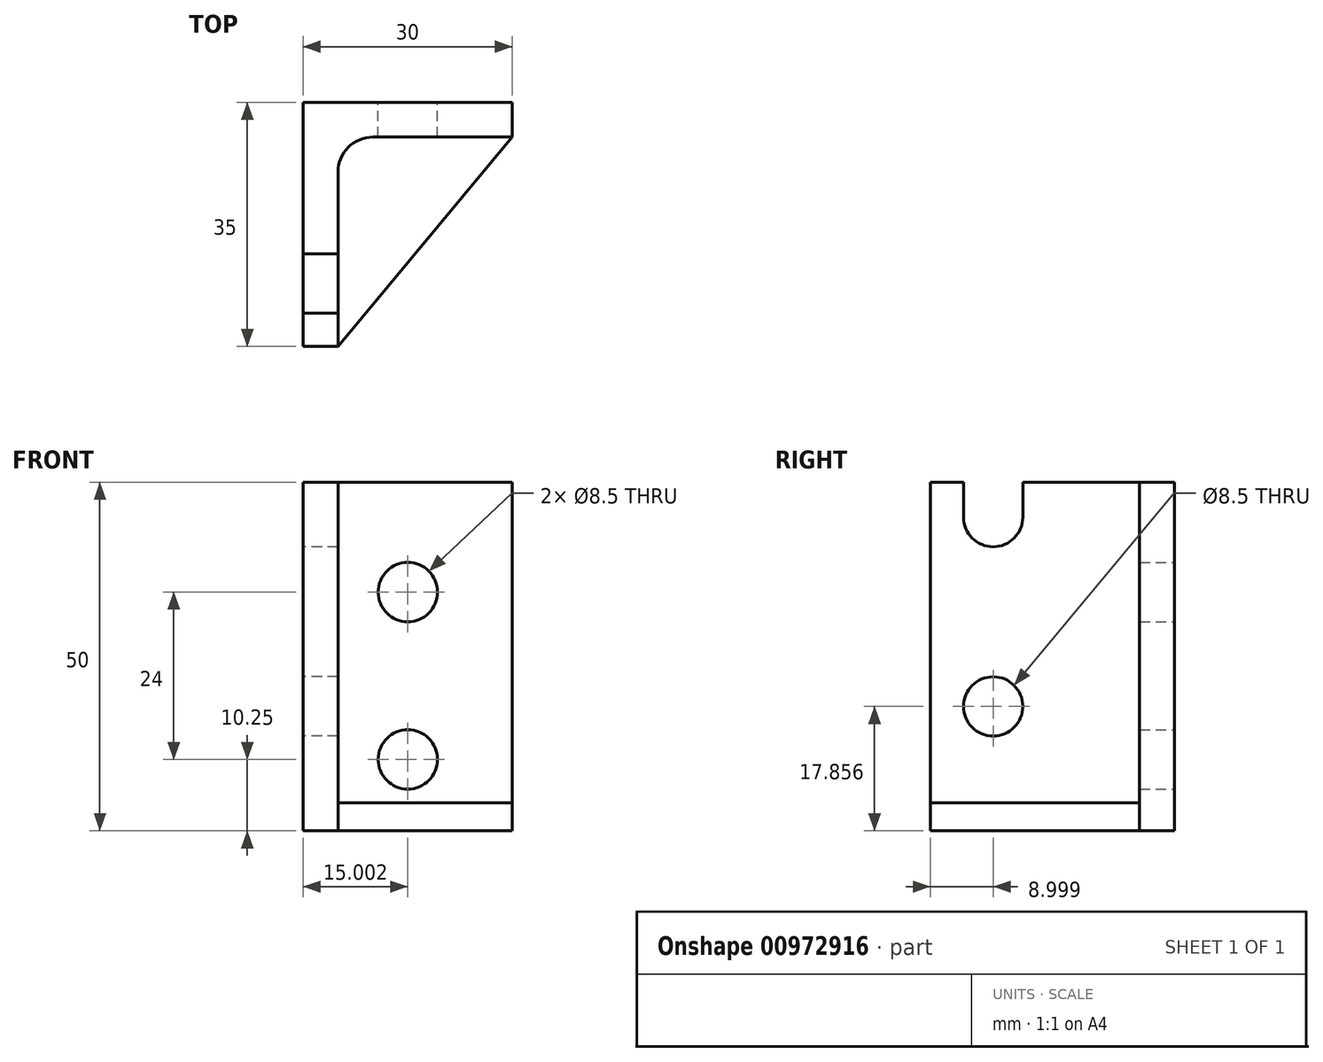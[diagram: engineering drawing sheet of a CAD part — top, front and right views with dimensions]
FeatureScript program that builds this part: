
annotation { "Feature Type Name" : "Feature", "Feature Type Description" : "" }
export const myFeature = defineFeature(function(context is Context, id is Id, definition is map)
    precondition{}
    {
        {
            var Q0;
            Q0=qCreatedBy(makeId("Top.planeOp"),FACE);
            var sketch = newSketch(context, id + "F0", { "sketchPlane" : qUnion([Q0])});
            skLineSegment(sketch, "E0", {"start": v(-9.75, -4.4) * mm, "end": v(-9.75, 25.6) * mm});
            skLineSegment(sketch, "E1", {"start": v(-9.75, 25.6) * mm, "end": v(15.25, 25.6) * mm});
            skLineSegment(sketch, "E2", {"start": v(-9.75, -4.4) * mm, "end": v(-14.75, -4.4) * mm});
            skLineSegment(sketch, "E3", {"start": v(-14.75, -4.4) * mm, "end": v(-14.75, 30.6) * mm});
            skLineSegment(sketch, "E4", {"start": v(-14.75, 30.6) * mm, "end": v(15.25, 30.6) * mm});
            skLineSegment(sketch, "E5", {"start": v(15.25, 30.6) * mm, "end": v(15.25, 25.6) * mm});
            skLineSegment(sketch, "E6", {"start": v(-9.75, -4.4) * mm, "end": v(15.25, 25.6) * mm});
            skSolve(sketch);
        }
        {
            var Q0;
            Q0=makeQuery(id+"F0.imprint","IMPRINT",FACE,{"disambiguationData":[TD([[makeQuery(id+"F0.imprint","IMPRINT",EDGE,{"derivedFrom":sQuery(id+"F0.wireOp",EDGE,"E0")}),1.0]])]});
            extrude(context, id + "F1", {"entities" : qUnion([Q0]), "depth" : 50 * mm, "offsetDistance" : 25 * mm});
        }
        {
            var Q0;
            Q0=makeQuery(id+"F0.imprint","IMPRINT",FACE,{"disambiguationData":[TD([[makeQuery(id+"F0.imprint","IMPRINT",EDGE,{"derivedFrom":sQuery(id+"F0.wireOp",EDGE,"E0")}),-1.0]])]});
            extrude(context, id + "F2", {"entities" : qUnion([Q0]), "operationType" : NewBodyOperationType.ADD, "depth" : 4 * mm, "offsetDistance" : 25 * mm});
        }
        {
            var Q0;
            Q0=makeQuery(id+"F1.opExtrude","SWEPT_FACE",FACE,{"disambiguationData":[OSD([sQuery(id+"F0.wireOp",EDGE,"E3")])]});
            var sketch = newSketch(context, id + "F3", { "sketchPlane" : qUnion([Q0])});
            skLineSegment(sketch, "E7.0.0", {"start": v(-30.6, 0) * mm, "end": v(4.4, 0) * mm});
            skLineSegment(sketch, "E7.0.1", {"start": v(4.4, 0) * mm, "end": v(4.4, 50) * mm});
            skLineSegment(sketch, "E7.0.2", {"start": v(4.4, 50) * mm, "end": v(-30.6, 50) * mm});
            skLineSegment(sketch, "E7.0.3", {"start": v(-30.6, 50) * mm, "end": v(-30.6, 0) * mm});
            skLineSegment(sketch, "E8", {"start": v(-30.6, 20) * mm, "end": v(4.4, 20) * mm, "construction": true});
            skLineSegment(sketch, "E9", {"start": v(-30.6, 45) * mm, "end": v(4.4, 45) * mm, "construction": true});
            skCircle(sketch, "E10", {"center": v(-4.6, 17.86) * mm, "radius": 4.25 * mm});
            skCircle(sketch, "E11", {"center": v(-4.6, 45) * mm, "radius": 4.25 * mm});
            skLineSegment(sketch, "E12", {"start": v(-0.35, 45) * mm, "end": v(-0.35, 50) * mm});
            skLineSegment(sketch, "E13", {"start": v(-8.85, 45) * mm, "end": v(-8.85, 50) * mm});
            skSolve(sketch);
        }
        {
            var Q0;
            Q0=makeQuery(id+"F3.imprint","IMPRINT",FACE,{"disambiguationData":[TD([[makeQuery(id+"F3.imprint","IMPRINT",EDGE,{"derivedFrom":sQuery(id+"F3.wireOp",EDGE,"E10")}),1.0]])]});
            var Q1;
            {var subQ0=sQuery(id+"F3.wireOp",EDGE,"E11");var subQ1=makeQuery(id+"F3.imprint","INTERSECT",VERTEX,{"derivedFrom":[subQ0,sQuery(id+"F3.wireOp",EDGE,"E12")]});Q1=makeQuery(id+"F3.imprint","IMPRINT",FACE,{"disambiguationData":[TD([[makeQuery(id+"F3.imprint","IMPRINT",EDGE,{"disambiguationData":[TD([[subQ1,-1.0]])],"derivedFrom":subQ0}),1.0]])]});}
            var Q2;
            {var subQ0=sQuery(id+"F3.wireOp",EDGE,"E12");Q2=makeQuery(id+"F3.imprint","IMPRINT",FACE,{"disambiguationData":[TD([[makeQuery(id+"F3.imprint","IMPRINT",EDGE,{"derivedFrom":subQ0}),1.0]])]});}
            extrude(context, id + "F4", {"entities" : qUnion([Q0, Q1, Q2]), "operationType" : NewBodyOperationType.REMOVE, "oppositeDirection" : true, "depth" : 25 * mm, "offsetDistance" : 25 * mm});
        }
        {
            var Q0;
            Q0=makeQuery(id+"F1.opExtrude","SWEPT_FACE",FACE,{"disambiguationData":[OSD([sQuery(id+"F0.wireOp",EDGE,"E4")])]});
            var sketch = newSketch(context, id + "F5", { "sketchPlane" : qUnion([Q0])});
            skLineSegment(sketch, "E14.0.0", {"start": v(-15.25, 0) * mm, "end": v(14.75, 0) * mm});
            skLineSegment(sketch, "E14.0.1", {"start": v(14.75, 0) * mm, "end": v(14.75, 50) * mm});
            skLineSegment(sketch, "E14.0.2", {"start": v(14.75, 50) * mm, "end": v(-15.25, 50) * mm});
            skLineSegment(sketch, "E14.0.3", {"start": v(-15.25, 50) * mm, "end": v(-15.25, 0) * mm});
            skCircle(sketch, "E15", {"center": v(-0.25, 10.25) * mm, "radius": 4.25 * mm});
            skCircle(sketch, "E16", {"center": v(-0.25, 34.25) * mm, "radius": 4.25 * mm});
            skPoint(sketch, "E17", {"position": v(-0.25, 0) * mm});
            skSolve(sketch);
        }
        {
            var Q0;
            Q0=makeQuery(id+"F5.imprint","IMPRINT",FACE,{"disambiguationData":[TD([[makeQuery(id+"F5.imprint","IMPRINT",EDGE,{"derivedFrom":sQuery(id+"F5.wireOp",EDGE,"E16")}),1.0]])]});
            var Q1;
            Q1=makeQuery(id+"F5.imprint","IMPRINT",FACE,{"disambiguationData":[TD([[makeQuery(id+"F5.imprint","IMPRINT",EDGE,{"derivedFrom":sQuery(id+"F5.wireOp",EDGE,"E15")}),1.0]])]});
            extrude(context, id + "F6", {"entities" : qUnion([Q0, Q1]), "operationType" : NewBodyOperationType.REMOVE, "oppositeDirection" : true, "depth" : 25 * mm, "offsetDistance" : 25 * mm});
        }
        {
            var Q0;
            Q0=makeQuery(id+"F1.opExtrude","SWEPT_EDGE",EDGE,{"disambiguationData":[OSD([sQuery(id+"F0.wireOp",EDGE,"E0"),sQuery(id+"F0.wireOp",EDGE,"E1")])]});
            fillet(context, id + "F7", {"entities" : qUnion([Q0]), "radius" : 5 * mm, "tangentPropagation" : true, "allowEdgeOverflow" : false});
        }
    });
